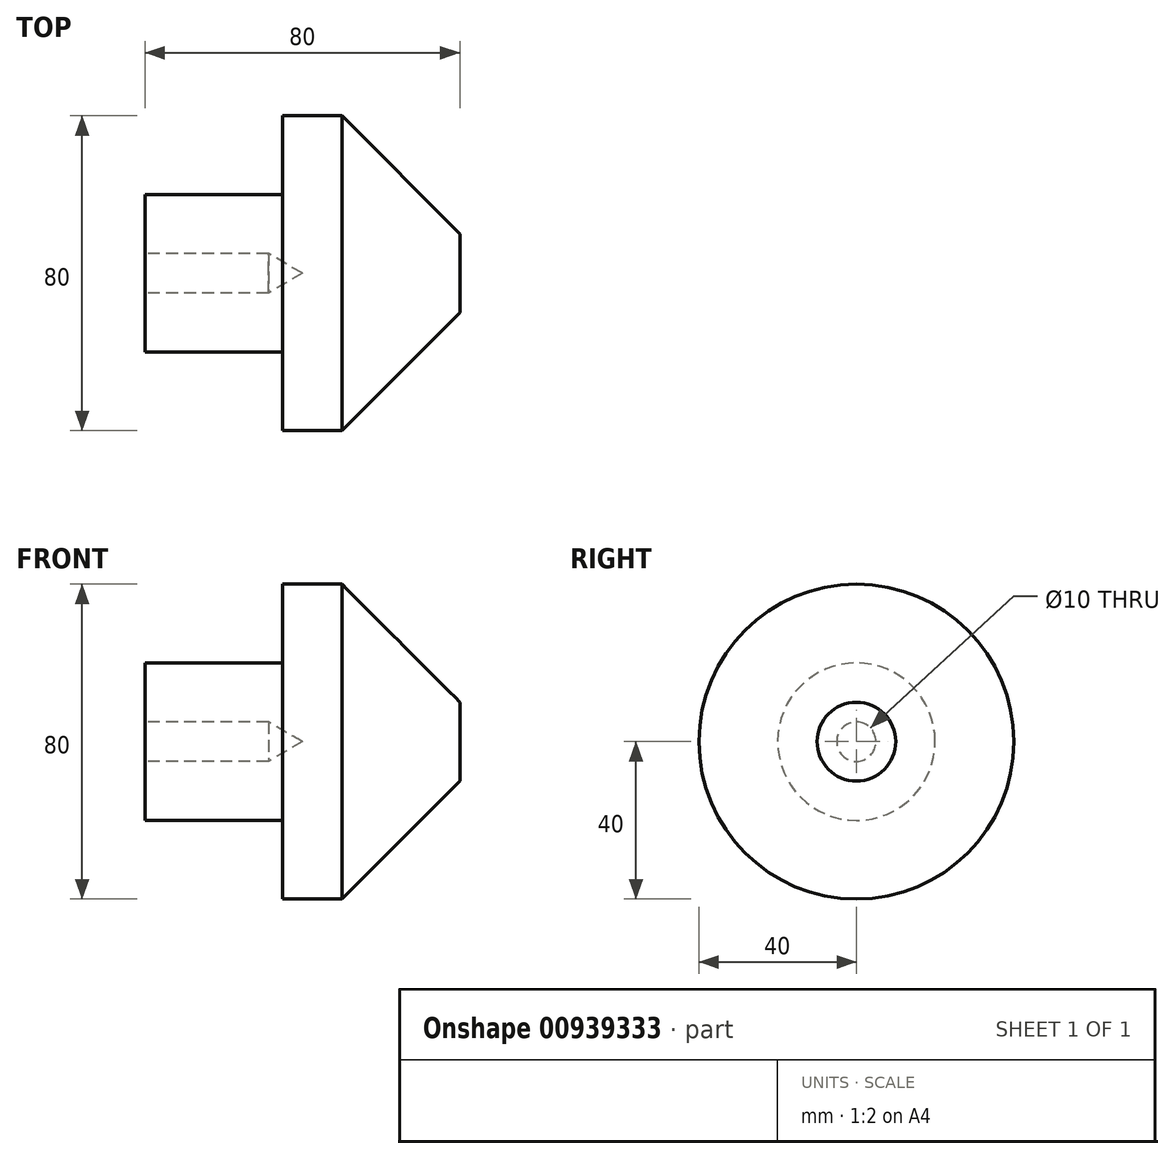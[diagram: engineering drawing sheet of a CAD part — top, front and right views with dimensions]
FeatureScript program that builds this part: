
annotation { "Feature Type Name" : "Feature", "Feature Type Description" : "" }
export const myFeature = defineFeature(function(context is Context, id is Id, definition is map)
    precondition{}
    {
        {
            var Q0;
            Q0=qCreatedBy(makeId("Top.planeOp"),FACE);
            var sketch = newSketch(context, id + "F0", { "sketchPlane" : qUnion([Q0])});
            skLineSegment(sketch, "E0", {"start": v(-102, 40) * mm, "end": v(-102, 20) * mm});
            skLineSegment(sketch, "E1", {"start": v(-102, 20) * mm, "end": v(-22, 20) * mm});
            skLineSegment(sketch, "E2", {"start": v(-22, 20) * mm, "end": v(-22, 30) * mm});
            skLineSegment(sketch, "E3", {"start": v(-22, 30) * mm, "end": v(-52, 60) * mm});
            skLineSegment(sketch, "E4", {"start": v(-52, 60) * mm, "end": v(-67, 60) * mm});
            skLineSegment(sketch, "E5", {"start": v(-67, 60) * mm, "end": v(-67, 40) * mm});
            skLineSegment(sketch, "E6", {"start": v(-67, 40) * mm, "end": v(-102, 40) * mm});
            skLineSegment(sketch, "E7", {"start": v(-102, 25) * mm, "end": v(-70.66, 25) * mm});
            skLineSegment(sketch, "E8", {"start": v(-70.66, 25) * mm, "end": v(-62, 20) * mm});
            skSolve(sketch);
        }
        {
            var Q0;
            {var subQ0=sQuery(id+"F0.wireOp",EDGE,"E2");Q0=makeQuery(id+"F0.imprint","IMPRINT",FACE,{"disambiguationData":[TD([[makeQuery(id+"F0.imprint","IMPRINT",EDGE,{"derivedFrom":subQ0}),1.0]])]});}
            var Q1;
            Q1=sQuery(id+"F0.wireOp",EDGE,"E1");
            revolve(context, id + "F1", {"surfaceOperationType" : NewSurfaceOperationType.NEW, "entities" : qUnion([Q0]), "axis" : qUnion([Q1]), "revolveType" : RevolveType.FULL});
        }
    });
